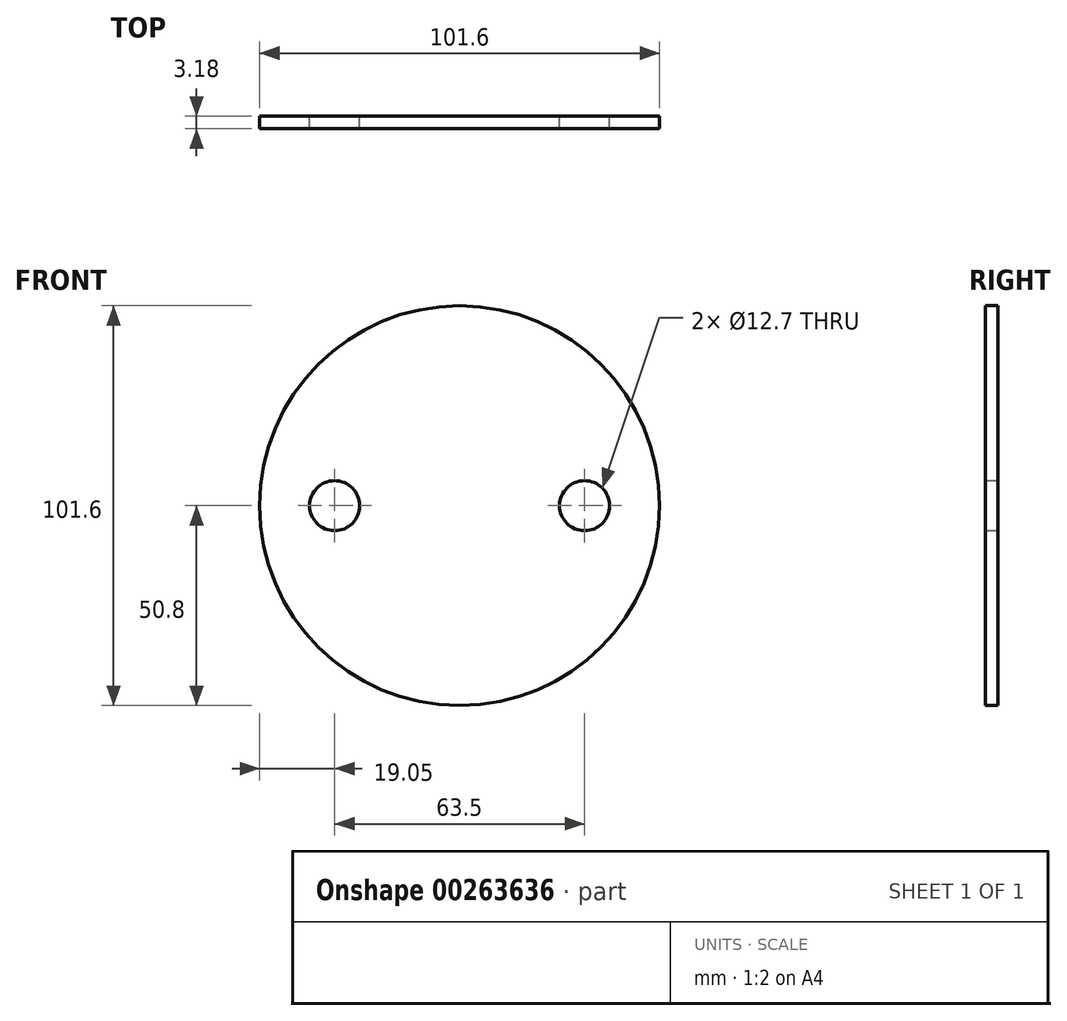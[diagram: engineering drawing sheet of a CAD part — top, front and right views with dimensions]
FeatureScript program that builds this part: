
annotation { "Feature Type Name" : "Feature", "Feature Type Description" : "" }
export const myFeature = defineFeature(function(context is Context, id is Id, definition is map)
    precondition{}
    {
        {
            var Q0;
            Q0=qCreatedBy(makeId("Front.planeOp"),FACE);
            var sketch = newSketch(context, id + "F0", { "sketchPlane" : qUnion([Q0])});
            skCircle(sketch, "E0", {"center": v(0, 0) * mm, "radius": 50.8 * mm});
            skLineSegment(sketch, "E1", {"start": v(-50.8, 0) * mm, "end": v(-31.75, 0) * mm});
            skPoint(sketch, "E2", {"position": v(31.75, 0) * mm});
            skCircle(sketch, "E3", {"center": v(31.75, 0) * mm, "radius": 6.35 * mm});
            skLineSegment(sketch, "E4", {"start": v(-50.8, 0) * mm, "end": v(-38.1, 0) * mm});
            skCircle(sketch, "E5", {"center": v(-31.75, 0) * mm, "radius": 6.35 * mm});
            skLineSegment(sketch, "E6.trimOffspring", {"start": v(-25.4, 0) * mm, "end": v(25.4, 0) * mm});
            skLineSegment(sketch, "E7.trimOffspring", {"start": v(38.1, 0) * mm, "end": v(50.8, 0) * mm});
            skSolve(sketch);
        }
        {
            var Q0;
            Q0=makeQuery(id+"F0.imprint","IMPRINT",FACE,{"disambiguationData":[TD([[makeQuery(id+"F0.imprint","IMPRINT",EDGE,{"derivedFrom":sQuery(id+"F0.wireOp",EDGE,"E0")}),1.0]])]});
            extrude(context, id + "F1", {"entities" : qUnion([Q0]), "depth" : 3.17 * mm});
        }
    });
